# Revit family: Patio-Door_Windsor_Novatech
name_source: partatom
category: Doors
units: mm (PartAtom-declared; Revit-internal decimal feet)

## family parameters
Always vertical = Yes
Classification Number = 23.30.10.00
Cut with Voids When Loaded = No
Host = Wall
Room Calculation Point = No
Shared = No

## types (3) — shared parameters
Analytic Construction = <None>
CAD Details = https://www.arcat.com
Define Thermal Properties by = Schematic Type
Frame Material = Aluminum
Function = Interior
Handle Height = 38"
Hardware Material = Aluminum
Height = 79 1/2"
Height Sash O = 76 1/4"
Height Sash X = 76 1/4"
Keynote = 08 32 00
Look Handle = Yes
Manufacturer = Novatech
Model = Windsor
Panel Material = Glass
Product Page URL = https://www.arcat.com
Rough Height = 80"
Specification = https://www.arcat.com
Thickness = 4 7/8"
URL = https://www.groupenovatech.com
View Handle = Yes
Wall Closure = By host

## per-type parameters (varying)
| type | Model_Sash to Reference Line | Rough Width | Width | Width Sash O | Width Sash X |
| 59 1/2"W X 79 1/2"H | 28 1/4" | 60" | 59 1/2" | 30 3/8" | 30 3/8" |
| 71 1/2"W X 79 1/2"H | 34 1/4" | 72" | 71 1/2" | 36 3/8" | 36 3/8" |
| 95 1/2"W X 79 1/2"H | 46 1/4" | 96" | 95 1/2" | 48 3/8" | 48 3/8" |

## geometry (parser evidence)
native form markers: Sweep x53
no freeform markers — native parametric forms only
